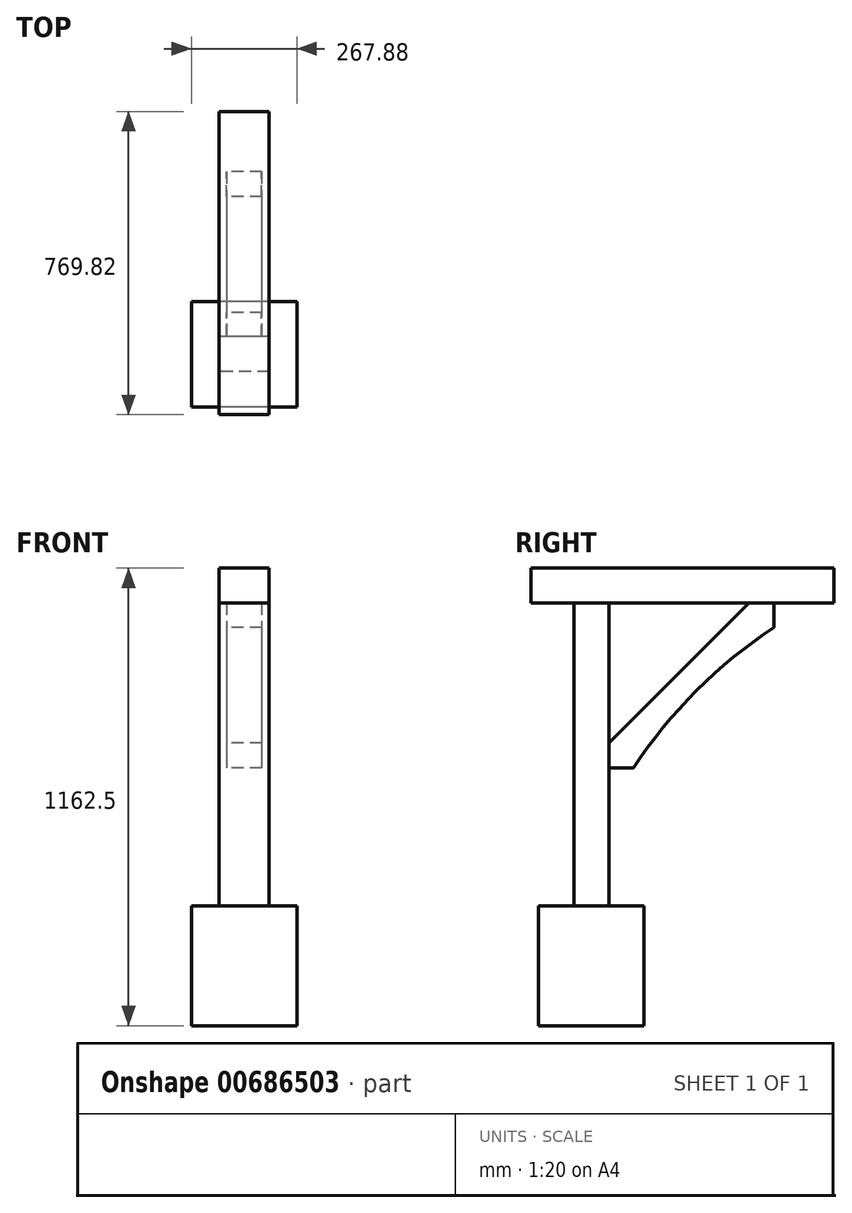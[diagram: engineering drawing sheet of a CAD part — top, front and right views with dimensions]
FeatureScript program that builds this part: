
annotation { "Feature Type Name" : "Feature", "Feature Type Description" : "" }
export const myFeature = defineFeature(function(context is Context, id is Id, definition is map)
    precondition{}
    {
        {
            var Q0;
            Q0=qCreatedBy(makeId("Right.planeOp"),FACE);
            var sketch = newSketch(context, id + "F0", { "sketchPlane" : qUnion([Q0])});
            skLineSegment(sketch, "E0", {"start": v(0, 0) * mm, "end": v(0, 1149.6) * mm, "construction": true});
            skLineSegment(sketch, "E1.bottom", {"start": v(-133.94, 0) * mm, "end": v(133.94, 0) * mm});
            skLineSegment(sketch, "E1.top", {"start": v(-133.94, 304.8) * mm, "end": v(133.94, 304.8) * mm});
            skLineSegment(sketch, "E1.left", {"start": v(-133.94, 0) * mm, "end": v(-133.94, 304.8) * mm});
            skLineSegment(sketch, "E1.right", {"start": v(133.94, 0) * mm, "end": v(133.94, 304.8) * mm});
            skLineSegment(sketch, "E2.bottom", {"start": v(-44.45, 1073.86) * mm, "end": v(44.45, 1073.86) * mm});
            skLineSegment(sketch, "E2.top", {"start": v(-44.45, 304.8) * mm, "end": v(44.45, 304.8) * mm});
            skLineSegment(sketch, "E2.left", {"start": v(-44.45, 1073.86) * mm, "end": v(-44.45, 304.8) * mm});
            skLineSegment(sketch, "E2.right", {"start": v(44.45, 1073.86) * mm, "end": v(44.45, 304.8) * mm});
            skLineSegment(sketch, "E3.bottom", {"start": v(-153.26, 1162.5) * mm, "end": v(616.56, 1162.5) * mm});
            skLineSegment(sketch, "E3.top", {"start": v(-153.26, 1073.86) * mm, "end": v(616.56, 1073.86) * mm});
            skLineSegment(sketch, "E3.left", {"start": v(-153.26, 1162.5) * mm, "end": v(-153.26, 1073.86) * mm});
            skLineSegment(sketch, "E3.right", {"start": v(616.56, 1162.5) * mm, "end": v(616.56, 1073.86) * mm});
            skLineSegment(sketch, "E4", {"start": v(400.05, 1073.86) * mm, "end": v(44.45, 718.26) * mm});
            skLineSegment(sketch, "E5", {"start": v(44.45, 654.76) * mm, "end": v(106.67, 654.76) * mm});
            skLineSegment(sketch, "E6", {"start": v(463.55, 1073.86) * mm, "end": v(463.55, 1011.64) * mm});
            skArc(sketch, "E7", {"start": v(463.55, 1011.64) * mm, "mid": v(267.15, 851.16) * mm, "end": v(106.67, 654.76) * mm});
            skLineSegment(sketch, "E8", {"start": v(44.45, 1073.86) * mm, "end": v(1162.53, -44.21) * mm, "construction": true});
            skPoint(sketch, "E9", {"position": v(222.25, 896.06) * mm});
            skLineSegment(sketch, "E10", {"start": v(106.67, 654.76) * mm, "end": v(463.55, 1011.64) * mm, "construction": true});
            skSolve(sketch);
        }
        {
            var Q0;
            Q0=qCreatedBy(makeId("Top.planeOp"),FACE);
            var sketch = newSketch(context, id + "F1", { "sketchPlane" : qUnion([Q0])});
            skLineSegment(sketch, "E11.bottom", {"start": v(133.94, 133.94) * mm, "end": v(-133.94, 133.94) * mm});
            skLineSegment(sketch, "E11.top", {"start": v(133.94, -133.94) * mm, "end": v(-133.94, -133.94) * mm});
            skLineSegment(sketch, "E11.left", {"start": v(133.94, 133.94) * mm, "end": v(133.94, -133.94) * mm});
            skLineSegment(sketch, "E11.right", {"start": v(-133.94, 133.94) * mm, "end": v(-133.94, -133.94) * mm});
            skPoint(sketch, "E11.middle", {"position": v(0, 0) * mm});
            skSolve(sketch);
        }
        {
            var Q0;
            Q0=makeQuery(id+"F1.imprint","IMPRINT",FACE,{"disambiguationData":[TD([[makeQuery(id+"F1.imprint","IMPRINT",EDGE,{"derivedFrom":sQuery(id+"F1.wireOp",EDGE,"E11.bottom")}),1.0]])]});
            var Q1;
            Q1=sQuery(id+"F0.wireOp",VERTEX,"E1.top.end");
            extrude(context, id + "F2", {"entities" : qUnion([Q0]), "endBound" : BoundingType.UP_TO_VERTEX, "depth" : 50.8 * mm, "endBoundEntityVertex" : qUnion([Q1]), "offsetDistance" : 25.4 * mm});
        }
        {
            var Q0;
            {var subQ1=sQuery(id+"F0.wireOp",EDGE,"E2.bottom");Q0=makeQuery(id+"F0.imprint","IMPRINT",FACE,{"disambiguationData":[TD([[makeQuery(id+"F0.imprint","IMPRINT",EDGE,{"derivedFrom":subQ1}),-1.0]])]});}
            extrude(context, id + "F3", {"entities" : qUnion([Q0]), "depth" : 127 * mm, "offsetDistance" : 25.4 * mm, "symmetric" : true});
        }
        {
            var Q0;
            {var subQ3=sQuery(id+"F0.wireOp",EDGE,"E2.bottom");Q0=makeQuery(id+"F0.imprint","IMPRINT",FACE,{"disambiguationData":[TD([[makeQuery(id+"F0.imprint","IMPRINT",EDGE,{"derivedFrom":subQ3}),1.0]])]});}
            var Q1;
            Q1=makeQuery(id+"F3.opExtrude","CAP_FACE",FACE,{"disambiguationData":[OSD([sQuery(id+"F0.wireOp",EDGE,"E1.top"),sQuery(id+"F0.wireOp",EDGE,"E2.bottom"),sQuery(id+"F0.wireOp",EDGE,"E2.left"),sQuery(id+"F0.wireOp",EDGE,"E2.right")])],"isStart":false});
            var Q2;
            Q2=makeQuery(id+"F3.opExtrude","CAP_FACE",FACE,{"disambiguationData":[OSD([sQuery(id+"F0.wireOp",EDGE,"E1.top"),sQuery(id+"F0.wireOp",EDGE,"E2.bottom"),sQuery(id+"F0.wireOp",EDGE,"E2.left"),sQuery(id+"F0.wireOp",EDGE,"E2.right")])],"isStart":true});
            extrude(context, id + "F4", {"entities" : qUnion([Q0]), "endBound" : BoundingType.UP_TO_SURFACE, "depth" : 25.4 * mm, "endBoundEntityFace" : qUnion([Q1]), "offsetDistance" : 25.4 * mm, "hasSecondDirection" : true, "secondDirectionBound" : BoundingType.UP_TO_SURFACE, "secondDirectionOppositeDirection" : true, "secondDirectionDepth" : 25.4 * mm, "secondDirectionBoundEntityFace" : qUnion([Q2])});
        }
        {
            var Q0;
            {var subQ1=sQuery(id+"F0.wireOp",EDGE,"E4");Q0=makeQuery(id+"F0.imprint","IMPRINT",FACE,{"disambiguationData":[TD([[makeQuery(id+"F0.imprint","IMPRINT",EDGE,{"derivedFrom":subQ1}),1.0]])]});}
            extrude(context, id + "F5", {"entities" : qUnion([Q0]), "depth" : 88.9 * mm, "offsetDistance" : 25.4 * mm, "symmetric" : true});
        }
    });
